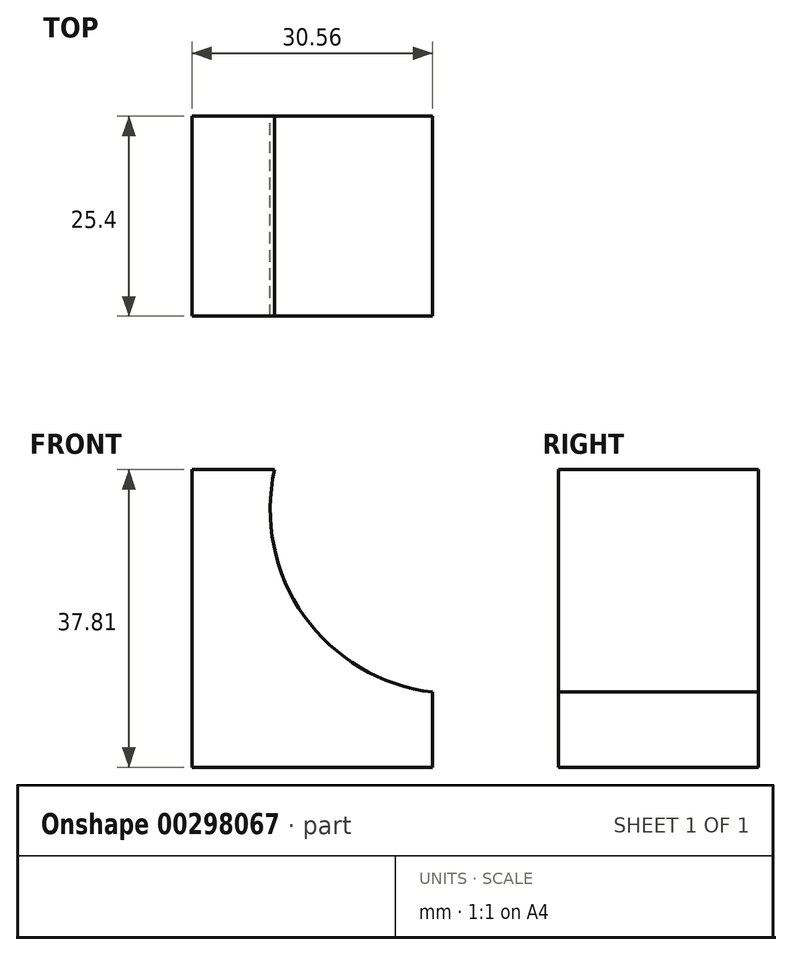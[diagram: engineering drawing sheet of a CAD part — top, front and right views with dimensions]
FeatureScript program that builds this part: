
annotation { "Feature Type Name" : "Feature", "Feature Type Description" : "" }
export const myFeature = defineFeature(function(context is Context, id is Id, definition is map)
    precondition{}
    {
        {
            var Q0;
            Q0=qCreatedBy(makeId("Front.planeOp"),FACE);
            var sketch = newSketch(context, id + "F0", { "sketchPlane" : qUnion([Q0])});
            skLineSegment(sketch, "E0", {"start": v(-63.02, 42.2) * mm, "end": v(-52.51, 42.2) * mm});
            skLineSegment(sketch, "E1", {"start": v(-63.02, 42.2) * mm, "end": v(-63.02, 4.4) * mm});
            skLineSegment(sketch, "E2", {"start": v(-63.02, 4.4) * mm, "end": v(-32.46, 4.4) * mm});
            skLineSegment(sketch, "E3", {"start": v(-32.46, 4.4) * mm, "end": v(-32.46, 13.94) * mm});
            skArc(sketch, "E4", {"start": v(-52.51, 42.2) * mm, "mid": v(-48.76, 23.62) * mm, "end": v(-32.46, 13.94) * mm});
            skSolve(sketch);
        }
        {
            var Q0;
            Q0 = qSketchRegion(id + "F0", true);
            extrude(context, id + "F1", {"entities" : qUnion([Q0]), "depth" : 25.4 * mm});
        }
    });
